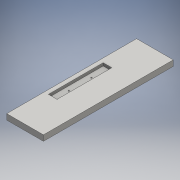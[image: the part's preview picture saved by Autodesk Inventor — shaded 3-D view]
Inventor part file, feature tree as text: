
AUTODESK INVENTOR PART (.ipt)
format: ipt  version: 2016 (Build 200138000, 138)  size: 118,784 bytes
history: native  units: mm
features: sketch x3, extrude x2, hole x1
ambient origin geometry x8: Origin, YZ Plane, XZ Plane, XY Plane, X Axis, Y Axis, Z Axis, Center Point
bodies: Solid1 (feature_tree)
feature tree (6):
  extrude  "baseExtrusion"  Depth=100.0mm
  hole  "xyStageAttatchM5"  [1 undecoded]
  extrude  "Extrusion2"  Depth=10.0mm
  sketch  "Sketch1"  dims[d0=30.0mm d1=100.0mm]
  sketch  "Sketch2"  dims[d2=460.0mm d3=230.0mm]
  sketch  "Sketch3"  dims[d4=10.0mm d5=0.0mm d6=80.0mm d7=40.0mm d8=30.0mm d9=30.0mm d10=4.134mm d11=10.0mm d12=4.0mm d13=2.0mm d14=90.0deg d15=14.2mm d16=20.594885mm d17=194.066919mm d18=97.033459mm d19=30.783029mm d20=15.391515mm d21=10.0mm d22=0.0mm]
note: 1 required parameter value undecoded (feature->parameter linkage not recoverable at this tier; creation-order binding heuristic only, values carry confidence <= 0.55)
